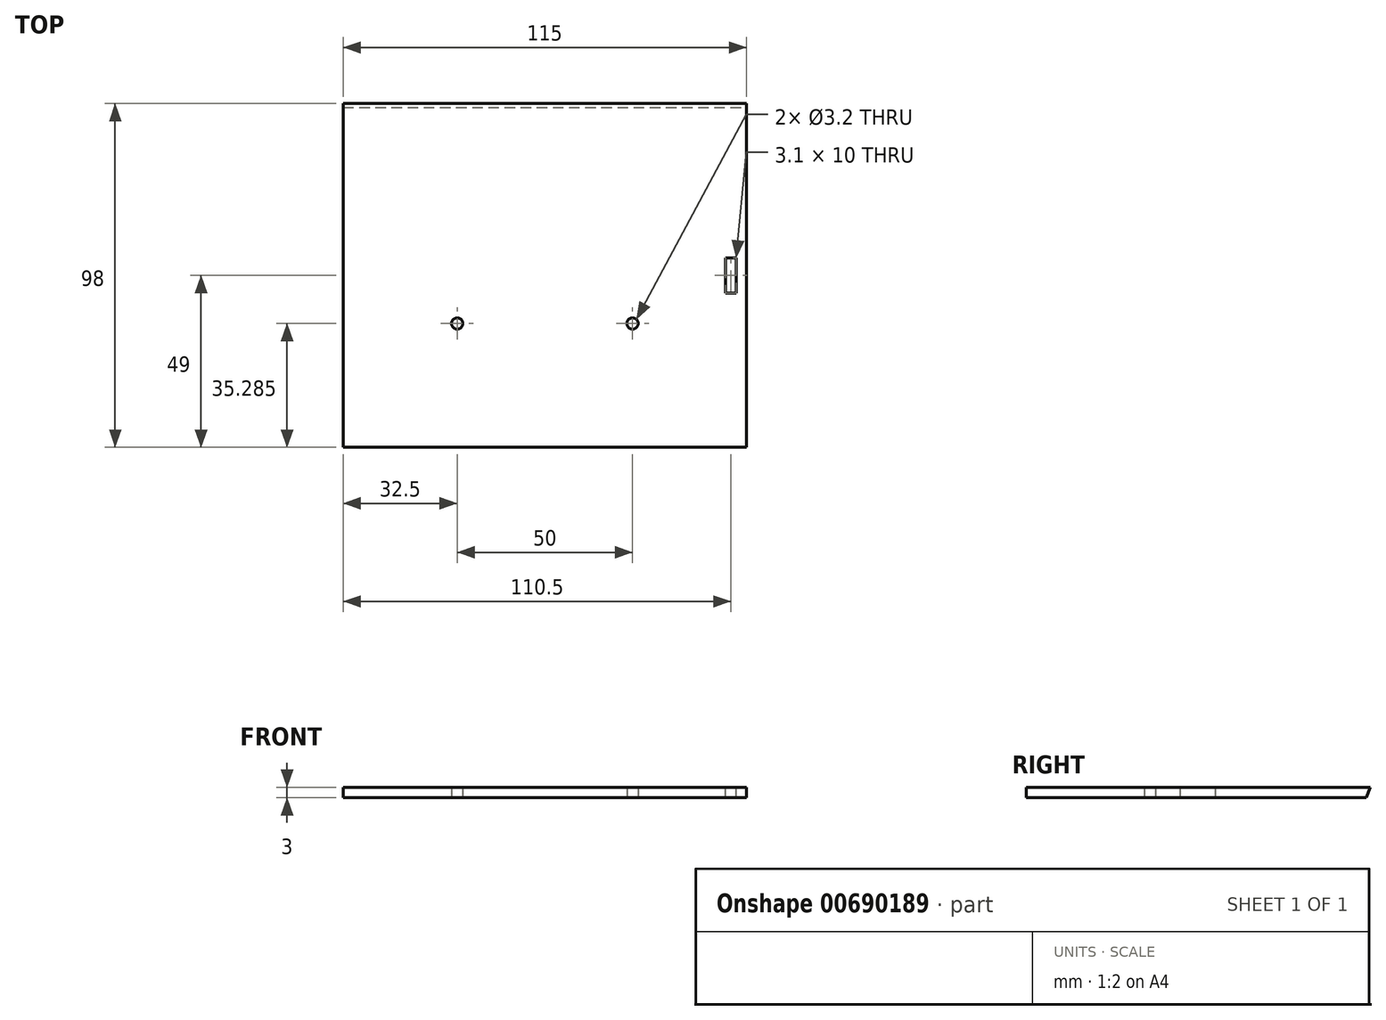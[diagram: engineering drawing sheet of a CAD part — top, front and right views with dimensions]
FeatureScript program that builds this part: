
annotation { "Feature Type Name" : "Feature", "Feature Type Description" : "" }
export const myFeature = defineFeature(function(context is Context, id is Id, definition is map)
    precondition{}
    {
        {
            var Q0;
            Q0=qCreatedBy(makeId("Top.planeOp"),FACE);
            var sketch = newSketch(context, id + "F0", { "sketchPlane" : qUnion([Q0])});
            skLineSegment(sketch, "E0.bottom", {"start": v(57.5, -49) * mm, "end": v(-57.5, -49) * mm});
            skLineSegment(sketch, "E0.top", {"start": v(57.5, 49) * mm, "end": v(-57.5, 49) * mm});
            skLineSegment(sketch, "E0.left", {"start": v(57.5, -49) * mm, "end": v(57.5, 49) * mm});
            skLineSegment(sketch, "E0.right", {"start": v(-57.5, -49) * mm, "end": v(-57.5, 49) * mm});
            skPoint(sketch, "E0.middle", {"position": v(0, 0) * mm});
            skSolve(sketch);
        }
        {
            var Q0;
            Q0=makeQuery(id+"F0.imprint","IMPRINT",FACE,{"disambiguationData":[TD([[makeQuery(id+"F0.imprint","IMPRINT",EDGE,{"derivedFrom":sQuery(id+"F0.wireOp",EDGE,"E0.bottom")}),-1.0]])]});
            extrude(context, id + "F1", {"entities" : qUnion([Q0]), "oppositeDirection" : true, "depth" : 3 * mm, "offsetDistance" : 25 * mm});
        }
        {
            var Q0;
            Q0=makeQuery(id+"F1.opExtrude","CAP_FACE",FACE,{"disambiguationData":[OSD([sQuery(id+"F0.wireOp",EDGE,"E0.bottom"),sQuery(id+"F0.wireOp",EDGE,"E0.top"),sQuery(id+"F0.wireOp",EDGE,"E0.left"),sQuery(id+"F0.wireOp",EDGE,"E0.right")])],"isStart":true});
            var sketch = newSketch(context, id + "F2", { "sketchPlane" : qUnion([Q0])});
            skLineSegment(sketch, "E1.bottom", {"start": v(54.55, -5) * mm, "end": v(51.45, -5) * mm});
            skLineSegment(sketch, "E1.top", {"start": v(54.55, 5) * mm, "end": v(51.45, 5) * mm});
            skLineSegment(sketch, "E1.left", {"start": v(54.55, -5) * mm, "end": v(54.55, 5) * mm});
            skLineSegment(sketch, "E1.right", {"start": v(51.45, -5) * mm, "end": v(51.45, 5) * mm});
            skPoint(sketch, "E1.middle", {"position": v(53, 0) * mm});
            skSolve(sketch);
        }
        {
            var Q0;
            Q0=makeQuery(id+"F2.imprint","IMPRINT",FACE,{"disambiguationData":[TD([[makeQuery(id+"F2.imprint","IMPRINT",EDGE,{"derivedFrom":sQuery(id+"F2.wireOp",EDGE,"E1.bottom")}),-1.0]])]});
            extrude(context, id + "F3", {"entities" : qUnion([Q0]), "operationType" : NewBodyOperationType.REMOVE, "endBound" : BoundingType.UP_TO_NEXT, "oppositeDirection" : true, "depth" : 25 * mm, "offsetDistance" : 25 * mm});
        }
        {
            var Q0;
            Q0=makeQuery(id+"F1.opExtrude","CAP_EDGE",EDGE,{"disambiguationData":[OSD([sQuery(id+"F0.wireOp",EDGE,"E0.top")])],"isStart":false});
            chamfer(context, id + "F4", {"entities" : qUnion([Q0]), "chamferType" : ChamferType.OFFSET_ANGLE, "width" : 3 * mm, "oppositeDirection" : false, "angle" : 20 * degree, "tangentPropagation" : true});
        }
        {
            var Q0;
            Q0=qCreatedBy(makeId("Right.planeOp"),FACE);
            var sketch = newSketch(context, id + "F5", { "sketchPlane" : qUnion([Q0])});
            skLineSegment(sketch, "E2", {"start": v(-48.98, -38.26) * mm, "end": v(-0.5, 10.21) * mm, "construction": true});
            skSolve(sketch);
        }
        {
            var Q0;
            Q0=sQuery(id+"F5.wireOp",EDGE,"E2");
            cPlane(context, id + "F6", {"entities" : qUnion([Q0]), "cplaneType" : CPlaneType.LINE_ANGLE, "offset" : 25 * mm, "angle" : 0 * degree, "width" : 150 * mm, "height" : 150 * mm});
        }
        {
            var Q0;
            Q0=makeQuery(id+"F1.opExtrude","CAP_FACE",FACE,{"disambiguationData":[OSD([sQuery(id+"F0.wireOp",EDGE,"E0.bottom"),sQuery(id+"F0.wireOp",EDGE,"E0.top"),sQuery(id+"F0.wireOp",EDGE,"E0.left"),sQuery(id+"F0.wireOp",EDGE,"E0.right")])],"isStart":false});
            var sketch = newSketch(context, id + "F7", { "sketchPlane" : qUnion([Q0])});
            skLineSegment(sketch, "E3", {"start": v(-107.68, 13.72) * mm, "end": v(133.05, 13.72) * mm, "construction": true});
            skPoint(sketch, "E4", {"position": v(25, 13.72) * mm});
            skPoint(sketch, "E5", {"position": v(-25, 13.72) * mm});
            skSolve(sketch);
        }
        {
            var Q0;
            Q0=sQuery(id+"F7.wireOp",VERTEX,"E4");
            var Q1;
            Q1=sQuery(id+"F7.wireOp",VERTEX,"E5");
            var Q2;
            Q2=makeQuery(id+"F1.opExtrude","SWEPT_BODY",BODY,{"disambiguationData":[OSD([sQuery(id+"F0.wireOp",EDGE,"E0.bottom"),sQuery(id+"F0.wireOp",EDGE,"E0.top"),sQuery(id+"F0.wireOp",EDGE,"E0.left"),sQuery(id+"F0.wireOp",EDGE,"E0.right")])]});
            hole(context, id + "F8", {"style" : HoleStyle.SIMPLE, "endStyle" : HoleEndStyle.BLIND, "holeDiameter" : 3.2 * mm, "majorDiameter" : 5 * mm, "holeDepth" : 5 * mm, "isTappedThrough" : true, "tappedDepth" : 2.3 * mm, "tapClearance" : 3, "startFromSketch" : true, "locations" : qUnion([Q0, Q1]), "scope" : qUnion([Q2])});
        }
    });
